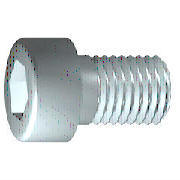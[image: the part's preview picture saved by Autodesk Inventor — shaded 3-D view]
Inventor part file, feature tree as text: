
AUTODESK INVENTOR PART (.ipt)
format: ipt  version: 2020 (Build 240168000, 168)  size: 198,656 bytes
history: native  units: mm (DEFAULTED — no unit token found)
features: sketch x2, extrude x1, plane x1, fillet x1
ambient origin geometry x7: Origin, YZ Plane, XY Plane, X Axis, Y Axis, Z Axis, Center Point
bodies: Solid1 (feature_tree), Body (feature_tree)
feature tree (5):
  extrude  "Slot"  Depth=2.8mm
  plane  "Work Plane1"
  fillet  "Fillet2"  Radius=2.8mm
  sketch  "Sketch1"  dims[d1=9.9mm d2=0.429515mm d3=2.8mm]
  sketch  "Sketch2"  dims[d4=2.3mm d5=60.0deg d6=4.0mm d7=4.0mm d8=2.886751mm d9=7.0mm d10=90.0deg d11=10.0mm d12=0.0mm d13=9.9mm d14=0.0mm d15=0.429415mm d16=0.429415mm d17=0.4mm d19=0.0mm d26=12.0mm d27=45.0deg d28=0.0mm d29=0.0mm d30=0.1mm]
